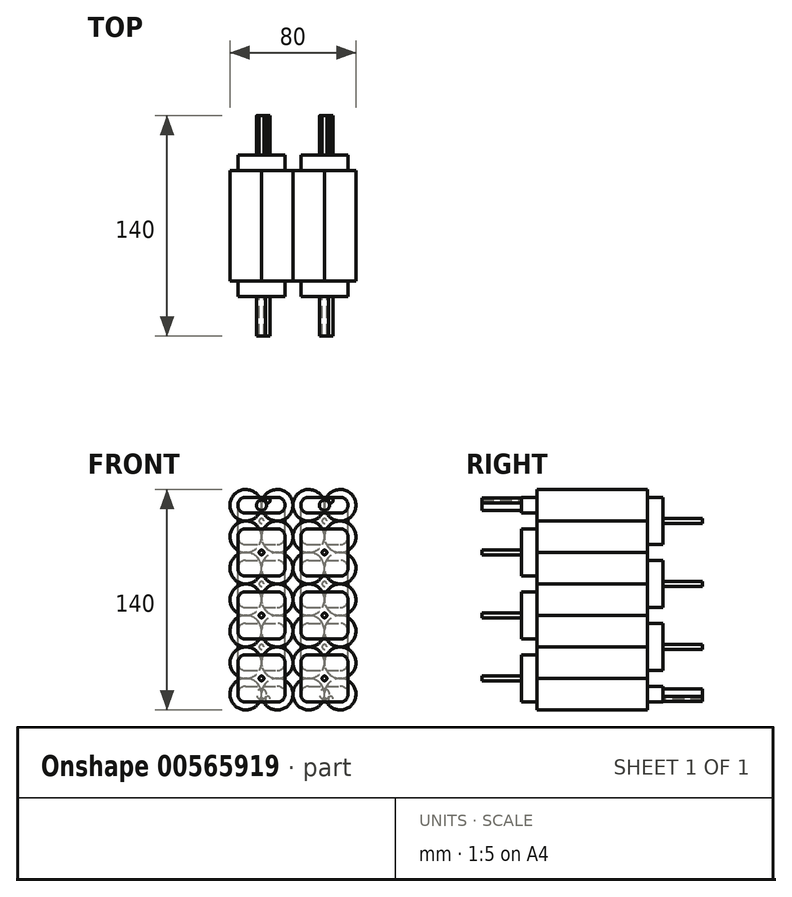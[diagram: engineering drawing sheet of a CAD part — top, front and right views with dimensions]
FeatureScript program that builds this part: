
annotation { "Feature Type Name" : "Feature", "Feature Type Description" : "" }
export const myFeature = defineFeature(function(context is Context, id is Id, definition is map)
    precondition{}
    {
        {
            var Q0;
            Q0=qCreatedBy(makeId("Front.planeOp"),FACE);
            var sketch = newSketch(context, id + "F0", { "sketchPlane" : qUnion([Q0])});
            skCircle(sketch, "E0", {"center": v(10, 10) * mm, "radius": 10 * mm});
            skCircle(sketch, "E1", {"center": v(30, 10) * mm, "radius": 10 * mm});
            skCircle(sketch, "E2", {"center": v(50, 10) * mm, "radius": 10 * mm});
            skCircle(sketch, "E3", {"center": v(70, 10) * mm, "radius": 10 * mm});
            skCircle(sketch, "E4", {"center": v(10, 30) * mm, "radius": 10 * mm});
            skCircle(sketch, "E5", {"center": v(30, 30) * mm, "radius": 10 * mm});
            skCircle(sketch, "E6", {"center": v(50, 30) * mm, "radius": 10 * mm});
            skCircle(sketch, "E7", {"center": v(70, 30) * mm, "radius": 10 * mm});
            skCircle(sketch, "E8", {"center": v(10, 50) * mm, "radius": 10 * mm});
            skCircle(sketch, "E9", {"center": v(30, 50) * mm, "radius": 10 * mm});
            skCircle(sketch, "E10", {"center": v(50, 50) * mm, "radius": 10 * mm});
            skCircle(sketch, "E11", {"center": v(70, 50) * mm, "radius": 10 * mm});
            skCircle(sketch, "E12", {"center": v(10, 70) * mm, "radius": 10 * mm});
            skCircle(sketch, "E13", {"center": v(30, 70) * mm, "radius": 10 * mm});
            skCircle(sketch, "E14", {"center": v(50, 70) * mm, "radius": 10 * mm});
            skCircle(sketch, "E15", {"center": v(70, 70) * mm, "radius": 10 * mm});
            skCircle(sketch, "E16", {"center": v(10, 90) * mm, "radius": 10 * mm});
            skCircle(sketch, "E17", {"center": v(30, 90) * mm, "radius": 10 * mm});
            skCircle(sketch, "E18", {"center": v(50, 90) * mm, "radius": 10 * mm});
            skCircle(sketch, "E19", {"center": v(70, 90) * mm, "radius": 10 * mm});
            skCircle(sketch, "E20", {"center": v(10, 110) * mm, "radius": 10 * mm});
            skCircle(sketch, "E21", {"center": v(30, 110) * mm, "radius": 10 * mm});
            skCircle(sketch, "E22", {"center": v(50, 110) * mm, "radius": 10 * mm});
            skCircle(sketch, "E23", {"center": v(70, 110) * mm, "radius": 10 * mm});
            skCircle(sketch, "E24", {"center": v(10, 130) * mm, "radius": 10 * mm});
            skCircle(sketch, "E25", {"center": v(30, 130) * mm, "radius": 10 * mm});
            skCircle(sketch, "E26", {"center": v(50, 130) * mm, "radius": 10 * mm});
            skCircle(sketch, "E27", {"center": v(70, 130) * mm, "radius": 10 * mm});
            skSolve(sketch);
        }
        {
            var Q0;
            Q0=qSketchRegion(id+"F0",true);
            extrude(context, id + "F1", {"entities" : qUnion([Q0]), "depth" : 70 * mm, "offsetDistance" : 25 * mm});
        }
        {
            var Q0;
            Q0=makeQuery(id+"F1.opExtrude","CAP_FACE",FACE,{"disambiguationData":[OSD([sQuery(id+"F0.wireOp",EDGE,"E27")])],"isStart":false});
            var sketch = newSketch(context, id + "F2", { "sketchPlane" : qUnion([Q0])});
            skLineSegment(sketch, "E28.bottom", {"start": v(35, 5) * mm, "end": v(5, 5) * mm});
            skLineSegment(sketch, "E28.top", {"start": v(35, 35) * mm, "end": v(5, 35) * mm});
            skLineSegment(sketch, "E28.left", {"start": v(35, 5) * mm, "end": v(35, 35) * mm});
            skLineSegment(sketch, "E28.right", {"start": v(5, 5) * mm, "end": v(5, 35) * mm});
            skPoint(sketch, "E28.middle", {"position": v(20, 20) * mm});
            skLineSegment(sketch, "E29.bottom", {"start": v(75, 5) * mm, "end": v(45, 5) * mm});
            skLineSegment(sketch, "E29.top", {"start": v(75, 35) * mm, "end": v(45, 35) * mm});
            skLineSegment(sketch, "E29.left", {"start": v(75, 5) * mm, "end": v(75, 35) * mm});
            skLineSegment(sketch, "E29.right", {"start": v(45, 5) * mm, "end": v(45, 35) * mm});
            skPoint(sketch, "E29.middle", {"position": v(60, 20) * mm});
            skLineSegment(sketch, "E30.bottom", {"start": v(35, 45) * mm, "end": v(5, 45) * mm});
            skLineSegment(sketch, "E30.top", {"start": v(35, 75) * mm, "end": v(5, 75) * mm});
            skLineSegment(sketch, "E30.left", {"start": v(35, 45) * mm, "end": v(35, 75) * mm});
            skLineSegment(sketch, "E30.right", {"start": v(5, 45) * mm, "end": v(5, 75) * mm});
            skPoint(sketch, "E30.middle", {"position": v(20, 60) * mm});
            skLineSegment(sketch, "E31.bottom", {"start": v(75, 45) * mm, "end": v(45, 45) * mm});
            skLineSegment(sketch, "E31.top", {"start": v(75, 75) * mm, "end": v(45, 75) * mm});
            skLineSegment(sketch, "E31.left", {"start": v(75, 45) * mm, "end": v(75, 75) * mm});
            skLineSegment(sketch, "E31.right", {"start": v(45, 45) * mm, "end": v(45, 75) * mm});
            skPoint(sketch, "E31.middle", {"position": v(60, 60) * mm});
            skLineSegment(sketch, "E32.bottom", {"start": v(35, 85) * mm, "end": v(5, 85) * mm});
            skLineSegment(sketch, "E32.top", {"start": v(35, 115) * mm, "end": v(5, 115) * mm});
            skLineSegment(sketch, "E32.left", {"start": v(35, 85) * mm, "end": v(35, 115) * mm});
            skLineSegment(sketch, "E32.right", {"start": v(5, 85) * mm, "end": v(5, 115) * mm});
            skPoint(sketch, "E32.middle", {"position": v(20, 100) * mm});
            skLineSegment(sketch, "E33.bottom", {"start": v(75, 85) * mm, "end": v(45, 85) * mm});
            skLineSegment(sketch, "E33.top", {"start": v(75, 115) * mm, "end": v(45, 115) * mm});
            skLineSegment(sketch, "E33.left", {"start": v(75, 85) * mm, "end": v(75, 115) * mm});
            skLineSegment(sketch, "E33.right", {"start": v(45, 85) * mm, "end": v(45, 115) * mm});
            skPoint(sketch, "E33.middle", {"position": v(60, 100) * mm});
            skLineSegment(sketch, "E34.bottom", {"start": v(35, 125) * mm, "end": v(5, 125) * mm});
            skLineSegment(sketch, "E34.top", {"start": v(35, 135) * mm, "end": v(5, 135) * mm});
            skLineSegment(sketch, "E34.left", {"start": v(35, 125) * mm, "end": v(35, 135) * mm});
            skLineSegment(sketch, "E34.right", {"start": v(5, 125) * mm, "end": v(5, 135) * mm});
            skPoint(sketch, "E34.middle", {"position": v(20, 130) * mm});
            skLineSegment(sketch, "E35.bottom", {"start": v(75, 125) * mm, "end": v(45, 125) * mm});
            skLineSegment(sketch, "E35.top", {"start": v(75, 135) * mm, "end": v(45, 135) * mm});
            skLineSegment(sketch, "E35.left", {"start": v(75, 125) * mm, "end": v(75, 135) * mm});
            skLineSegment(sketch, "E35.right", {"start": v(45, 125) * mm, "end": v(45, 135) * mm});
            skPoint(sketch, "E35.middle", {"position": v(60, 130) * mm});
            skSolve(sketch);
        }
        {
            var Q0;
            Q0 = qSketchRegion(id + "F2", true);
            extrude(context, id + "F3", {"entities" : qUnion([Q0]), "depth" : 10 * mm, "offsetDistance" : 25 * mm});
        }
        {
            var Q0;
            Q0=makeQuery(id+"F1.opExtrude","CAP_FACE",FACE,{"disambiguationData":[OSD([sQuery(id+"F0.wireOp",EDGE,"E24")])],"isStart":true});
            var sketch = newSketch(context, id + "F4", { "sketchPlane" : qUnion([Q0])});
            skLineSegment(sketch, "E36.bottom", {"start": v(-45, 25) * mm, "end": v(-75, 25) * mm});
            skLineSegment(sketch, "E36.top", {"start": v(-45, 55) * mm, "end": v(-75, 55) * mm});
            skLineSegment(sketch, "E36.left", {"start": v(-45, 25) * mm, "end": v(-45, 55) * mm});
            skLineSegment(sketch, "E36.right", {"start": v(-75, 25) * mm, "end": v(-75, 55) * mm});
            skPoint(sketch, "E36.middle", {"position": v(-60, 40) * mm});
            skLineSegment(sketch, "E37.bottom", {"start": v(-5, 25) * mm, "end": v(-35, 25) * mm});
            skLineSegment(sketch, "E37.top", {"start": v(-5, 55) * mm, "end": v(-35, 55) * mm});
            skLineSegment(sketch, "E37.left", {"start": v(-5, 25) * mm, "end": v(-5, 55) * mm});
            skLineSegment(sketch, "E37.right", {"start": v(-35, 25) * mm, "end": v(-35, 55) * mm});
            skPoint(sketch, "E37.middle", {"position": v(-20, 40) * mm});
            skLineSegment(sketch, "E38.bottom", {"start": v(-45, 65) * mm, "end": v(-75, 65) * mm});
            skLineSegment(sketch, "E38.top", {"start": v(-45, 95) * mm, "end": v(-75, 95) * mm});
            skLineSegment(sketch, "E38.left", {"start": v(-45, 65) * mm, "end": v(-45, 95) * mm});
            skLineSegment(sketch, "E38.right", {"start": v(-75, 65) * mm, "end": v(-75, 95) * mm});
            skPoint(sketch, "E38.middle", {"position": v(-60, 80) * mm});
            skLineSegment(sketch, "E39.bottom", {"start": v(-5, 65) * mm, "end": v(-35, 65) * mm});
            skLineSegment(sketch, "E39.top", {"start": v(-5, 95) * mm, "end": v(-35, 95) * mm});
            skLineSegment(sketch, "E39.left", {"start": v(-5, 65) * mm, "end": v(-5, 95) * mm});
            skLineSegment(sketch, "E39.right", {"start": v(-35, 65) * mm, "end": v(-35, 95) * mm});
            skPoint(sketch, "E39.middle", {"position": v(-20, 80) * mm});
            skLineSegment(sketch, "E40.bottom", {"start": v(-45, 105) * mm, "end": v(-75, 105) * mm});
            skLineSegment(sketch, "E40.top", {"start": v(-45, 135) * mm, "end": v(-75, 135) * mm});
            skLineSegment(sketch, "E40.left", {"start": v(-45, 105) * mm, "end": v(-45, 135) * mm});
            skLineSegment(sketch, "E40.right", {"start": v(-75, 105) * mm, "end": v(-75, 135) * mm});
            skPoint(sketch, "E40.middle", {"position": v(-60, 120) * mm});
            skLineSegment(sketch, "E41.bottom", {"start": v(-5, 105) * mm, "end": v(-35, 105) * mm});
            skLineSegment(sketch, "E41.top", {"start": v(-5, 135) * mm, "end": v(-35, 135) * mm});
            skLineSegment(sketch, "E41.left", {"start": v(-5, 105) * mm, "end": v(-5, 135) * mm});
            skLineSegment(sketch, "E41.right", {"start": v(-35, 105) * mm, "end": v(-35, 135) * mm});
            skPoint(sketch, "E41.middle", {"position": v(-20, 120) * mm});
            skLineSegment(sketch, "E42.bottom", {"start": v(-45, 5) * mm, "end": v(-75, 5) * mm});
            skLineSegment(sketch, "E42.top", {"start": v(-45, 15) * mm, "end": v(-75, 15) * mm});
            skLineSegment(sketch, "E42.left", {"start": v(-45, 5) * mm, "end": v(-45, 15) * mm});
            skLineSegment(sketch, "E42.right", {"start": v(-75, 5) * mm, "end": v(-75, 15) * mm});
            skPoint(sketch, "E42.middle", {"position": v(-60, 10) * mm});
            skLineSegment(sketch, "E43.bottom", {"start": v(-5, 5) * mm, "end": v(-35, 5) * mm});
            skLineSegment(sketch, "E43.top", {"start": v(-5, 15) * mm, "end": v(-35, 15) * mm});
            skLineSegment(sketch, "E43.left", {"start": v(-5, 5) * mm, "end": v(-5, 15) * mm});
            skLineSegment(sketch, "E43.right", {"start": v(-35, 5) * mm, "end": v(-35, 15) * mm});
            skPoint(sketch, "E43.middle", {"position": v(-20, 10) * mm});
            skSolve(sketch);
        }
        {
            var Q0;
            Q0 = qSketchRegion(id + "F4", true);
            extrude(context, id + "F5", {"entities" : qUnion([Q0]), "depth" : 10 * mm, "offsetDistance" : 25 * mm});
        }
        {
            var Q0;
            Q0=makeQuery(id+"F3.opExtrude","SWEPT_EDGE",EDGE,{"disambiguationData":[OSD([sQuery(id+"F2.wireOp",EDGE,"E35.top"),sQuery(id+"F2.wireOp",EDGE,"E35.left")])]});
            var Q1;
            Q1=makeQuery(id+"F3.opExtrude","SWEPT_EDGE",EDGE,{"disambiguationData":[OSD([sQuery(id+"F2.wireOp",EDGE,"E35.bottom"),sQuery(id+"F2.wireOp",EDGE,"E35.left")])]});
            var Q2;
            Q2=makeQuery(id+"F3.opExtrude","SWEPT_EDGE",EDGE,{"disambiguationData":[OSD([sQuery(id+"F2.wireOp",EDGE,"E33.top"),sQuery(id+"F2.wireOp",EDGE,"E33.left")])]});
            var Q3;
            Q3=makeQuery(id+"F3.opExtrude","SWEPT_EDGE",EDGE,{"disambiguationData":[OSD([sQuery(id+"F2.wireOp",EDGE,"E33.bottom"),sQuery(id+"F2.wireOp",EDGE,"E33.left")])]});
            var Q4;
            Q4=makeQuery(id+"F3.opExtrude","SWEPT_EDGE",EDGE,{"disambiguationData":[OSD([sQuery(id+"F2.wireOp",EDGE,"E33.top"),sQuery(id+"F2.wireOp",EDGE,"E33.right")])]});
            var Q5;
            Q5=makeQuery(id+"F3.opExtrude","SWEPT_EDGE",EDGE,{"disambiguationData":[OSD([sQuery(id+"F2.wireOp",EDGE,"E35.top"),sQuery(id+"F2.wireOp",EDGE,"E35.right")])]});
            var Q6;
            Q6=makeQuery(id+"F3.opExtrude","SWEPT_EDGE",EDGE,{"disambiguationData":[OSD([sQuery(id+"F2.wireOp",EDGE,"E34.top"),sQuery(id+"F2.wireOp",EDGE,"E34.left")])]});
            var Q7;
            Q7=makeQuery(id+"F3.opExtrude","SWEPT_EDGE",EDGE,{"disambiguationData":[OSD([sQuery(id+"F2.wireOp",EDGE,"E34.top"),sQuery(id+"F2.wireOp",EDGE,"E34.right")])]});
            var Q8;
            Q8=makeQuery(id+"F3.opExtrude","SWEPT_EDGE",EDGE,{"disambiguationData":[OSD([sQuery(id+"F2.wireOp",EDGE,"E32.top"),sQuery(id+"F2.wireOp",EDGE,"E32.right")])]});
            var Q9;
            Q9=makeQuery(id+"F3.opExtrude","SWEPT_EDGE",EDGE,{"disambiguationData":[OSD([sQuery(id+"F2.wireOp",EDGE,"E32.top"),sQuery(id+"F2.wireOp",EDGE,"E32.left")])]});
            var Q10;
            Q10=makeQuery(id+"F3.opExtrude","SWEPT_EDGE",EDGE,{"disambiguationData":[OSD([sQuery(id+"F2.wireOp",EDGE,"E30.top"),sQuery(id+"F2.wireOp",EDGE,"E30.right")])]});
            var Q11;
            Q11=makeQuery(id+"F3.opExtrude","SWEPT_EDGE",EDGE,{"disambiguationData":[OSD([sQuery(id+"F2.wireOp",EDGE,"E30.top"),sQuery(id+"F2.wireOp",EDGE,"E30.left")])]});
            var Q12;
            Q12=makeQuery(id+"F3.opExtrude","SWEPT_EDGE",EDGE,{"disambiguationData":[OSD([sQuery(id+"F2.wireOp",EDGE,"E31.top"),sQuery(id+"F2.wireOp",EDGE,"E31.right")])]});
            var Q13;
            Q13=makeQuery(id+"F3.opExtrude","SWEPT_EDGE",EDGE,{"disambiguationData":[OSD([sQuery(id+"F2.wireOp",EDGE,"E31.top"),sQuery(id+"F2.wireOp",EDGE,"E31.left")])]});
            var Q14;
            Q14=makeQuery(id+"F3.opExtrude","SWEPT_EDGE",EDGE,{"disambiguationData":[OSD([sQuery(id+"F2.wireOp",EDGE,"E31.bottom"),sQuery(id+"F2.wireOp",EDGE,"E31.left")])]});
            var Q15;
            Q15=makeQuery(id+"F3.opExtrude","SWEPT_EDGE",EDGE,{"disambiguationData":[OSD([sQuery(id+"F2.wireOp",EDGE,"E30.bottom"),sQuery(id+"F2.wireOp",EDGE,"E30.left")])]});
            var Q16;
            Q16=makeQuery(id+"F3.opExtrude","SWEPT_EDGE",EDGE,{"disambiguationData":[OSD([sQuery(id+"F2.wireOp",EDGE,"E34.bottom"),sQuery(id+"F2.wireOp",EDGE,"E34.left")])]});
            var Q17;
            Q17=makeQuery(id+"F3.opExtrude","SWEPT_EDGE",EDGE,{"disambiguationData":[OSD([sQuery(id+"F2.wireOp",EDGE,"E32.bottom"),sQuery(id+"F2.wireOp",EDGE,"E32.left")])]});
            var Q18;
            Q18=makeQuery(id+"F3.opExtrude","SWEPT_EDGE",EDGE,{"disambiguationData":[OSD([sQuery(id+"F2.wireOp",EDGE,"E28.top"),sQuery(id+"F2.wireOp",EDGE,"E28.right")])]});
            var Q19;
            Q19=makeQuery(id+"F3.opExtrude","SWEPT_EDGE",EDGE,{"disambiguationData":[OSD([sQuery(id+"F2.wireOp",EDGE,"E28.top"),sQuery(id+"F2.wireOp",EDGE,"E28.left")])]});
            var Q20;
            Q20=makeQuery(id+"F3.opExtrude","SWEPT_EDGE",EDGE,{"disambiguationData":[OSD([sQuery(id+"F2.wireOp",EDGE,"E29.top"),sQuery(id+"F2.wireOp",EDGE,"E29.right")])]});
            var Q21;
            Q21=makeQuery(id+"F3.opExtrude","SWEPT_EDGE",EDGE,{"disambiguationData":[OSD([sQuery(id+"F2.wireOp",EDGE,"E29.top"),sQuery(id+"F2.wireOp",EDGE,"E29.left")])]});
            var Q22;
            Q22=makeQuery(id+"F3.opExtrude","SWEPT_EDGE",EDGE,{"disambiguationData":[OSD([sQuery(id+"F2.wireOp",EDGE,"E29.bottom"),sQuery(id+"F2.wireOp",EDGE,"E29.left")])]});
            var Q23;
            Q23=makeQuery(id+"F3.opExtrude","SWEPT_EDGE",EDGE,{"disambiguationData":[OSD([sQuery(id+"F2.wireOp",EDGE,"E28.bottom"),sQuery(id+"F2.wireOp",EDGE,"E28.left")])]});
            var Q24;
            Q24=makeQuery(id+"F3.opExtrude","SWEPT_EDGE",EDGE,{"disambiguationData":[OSD([sQuery(id+"F2.wireOp",EDGE,"E34.bottom"),sQuery(id+"F2.wireOp",EDGE,"E34.right")])]});
            var Q25;
            Q25=makeQuery(id+"F3.opExtrude","SWEPT_EDGE",EDGE,{"disambiguationData":[OSD([sQuery(id+"F2.wireOp",EDGE,"E35.bottom"),sQuery(id+"F2.wireOp",EDGE,"E35.right")])]});
            var Q26;
            Q26=makeQuery(id+"F3.opExtrude","SWEPT_EDGE",EDGE,{"disambiguationData":[OSD([sQuery(id+"F2.wireOp",EDGE,"E32.bottom"),sQuery(id+"F2.wireOp",EDGE,"E32.right")])]});
            var Q27;
            Q27=makeQuery(id+"F3.opExtrude","SWEPT_EDGE",EDGE,{"disambiguationData":[OSD([sQuery(id+"F2.wireOp",EDGE,"E33.bottom"),sQuery(id+"F2.wireOp",EDGE,"E33.right")])]});
            var Q28;
            Q28=makeQuery(id+"F3.opExtrude","SWEPT_EDGE",EDGE,{"disambiguationData":[OSD([sQuery(id+"F2.wireOp",EDGE,"E30.bottom"),sQuery(id+"F2.wireOp",EDGE,"E30.right")])]});
            var Q29;
            Q29=makeQuery(id+"F3.opExtrude","SWEPT_EDGE",EDGE,{"disambiguationData":[OSD([sQuery(id+"F2.wireOp",EDGE,"E31.bottom"),sQuery(id+"F2.wireOp",EDGE,"E31.right")])]});
            var Q30;
            Q30=makeQuery(id+"F3.opExtrude","SWEPT_EDGE",EDGE,{"disambiguationData":[OSD([sQuery(id+"F2.wireOp",EDGE,"E28.bottom"),sQuery(id+"F2.wireOp",EDGE,"E28.right")])]});
            var Q31;
            Q31=makeQuery(id+"F3.opExtrude","SWEPT_EDGE",EDGE,{"disambiguationData":[OSD([sQuery(id+"F2.wireOp",EDGE,"E29.bottom"),sQuery(id+"F2.wireOp",EDGE,"E29.right")])]});
            var Q32;
            Q32=makeQuery(id+"F5.opExtrude","SWEPT_EDGE",EDGE,{"disambiguationData":[OSD([sQuery(id+"F4.wireOp",EDGE,"E43.bottom"),sQuery(id+"F4.wireOp",EDGE,"E43.left")])]});
            var Q33;
            Q33=makeQuery(id+"F5.opExtrude","SWEPT_EDGE",EDGE,{"disambiguationData":[OSD([sQuery(id+"F4.wireOp",EDGE,"E37.bottom"),sQuery(id+"F4.wireOp",EDGE,"E37.left")])]});
            var Q34;
            Q34=makeQuery(id+"F5.opExtrude","SWEPT_EDGE",EDGE,{"disambiguationData":[OSD([sQuery(id+"F4.wireOp",EDGE,"E43.bottom"),sQuery(id+"F4.wireOp",EDGE,"E43.right")])]});
            var Q35;
            Q35=makeQuery(id+"F5.opExtrude","SWEPT_EDGE",EDGE,{"disambiguationData":[OSD([sQuery(id+"F4.wireOp",EDGE,"E42.bottom"),sQuery(id+"F4.wireOp",EDGE,"E42.left")])]});
            var Q36;
            Q36=makeQuery(id+"F5.opExtrude","SWEPT_EDGE",EDGE,{"disambiguationData":[OSD([sQuery(id+"F4.wireOp",EDGE,"E42.top"),sQuery(id+"F4.wireOp",EDGE,"E42.left")])]});
            var Q37;
            Q37=makeQuery(id+"F5.opExtrude","SWEPT_EDGE",EDGE,{"disambiguationData":[OSD([sQuery(id+"F4.wireOp",EDGE,"E37.bottom"),sQuery(id+"F4.wireOp",EDGE,"E37.right")])]});
            var Q38;
            Q38=makeQuery(id+"F5.opExtrude","SWEPT_EDGE",EDGE,{"disambiguationData":[OSD([sQuery(id+"F4.wireOp",EDGE,"E36.bottom"),sQuery(id+"F4.wireOp",EDGE,"E36.left")])]});
            var Q39;
            Q39=makeQuery(id+"F5.opExtrude","SWEPT_EDGE",EDGE,{"disambiguationData":[OSD([sQuery(id+"F4.wireOp",EDGE,"E42.bottom"),sQuery(id+"F4.wireOp",EDGE,"E42.right")])]});
            var Q40;
            Q40=makeQuery(id+"F5.opExtrude","SWEPT_EDGE",EDGE,{"disambiguationData":[OSD([sQuery(id+"F4.wireOp",EDGE,"E36.bottom"),sQuery(id+"F4.wireOp",EDGE,"E36.right")])]});
            var Q41;
            Q41=makeQuery(id+"F5.opExtrude","SWEPT_EDGE",EDGE,{"disambiguationData":[OSD([sQuery(id+"F4.wireOp",EDGE,"E36.top"),sQuery(id+"F4.wireOp",EDGE,"E36.left")])]});
            var Q42;
            Q42=makeQuery(id+"F5.opExtrude","SWEPT_EDGE",EDGE,{"disambiguationData":[OSD([sQuery(id+"F4.wireOp",EDGE,"E38.bottom"),sQuery(id+"F4.wireOp",EDGE,"E38.right")])]});
            var Q43;
            Q43=makeQuery(id+"F5.opExtrude","SWEPT_EDGE",EDGE,{"disambiguationData":[OSD([sQuery(id+"F4.wireOp",EDGE,"E38.bottom"),sQuery(id+"F4.wireOp",EDGE,"E38.left")])]});
            var Q44;
            Q44=makeQuery(id+"F5.opExtrude","SWEPT_EDGE",EDGE,{"disambiguationData":[OSD([sQuery(id+"F4.wireOp",EDGE,"E39.bottom"),sQuery(id+"F4.wireOp",EDGE,"E39.right")])]});
            var Q45;
            Q45=makeQuery(id+"F5.opExtrude","SWEPT_EDGE",EDGE,{"disambiguationData":[OSD([sQuery(id+"F4.wireOp",EDGE,"E38.top"),sQuery(id+"F4.wireOp",EDGE,"E38.left")])]});
            var Q46;
            Q46=makeQuery(id+"F5.opExtrude","SWEPT_EDGE",EDGE,{"disambiguationData":[OSD([sQuery(id+"F4.wireOp",EDGE,"E39.bottom"),sQuery(id+"F4.wireOp",EDGE,"E39.left")])]});
            var Q47;
            Q47=makeQuery(id+"F5.opExtrude","SWEPT_EDGE",EDGE,{"disambiguationData":[OSD([sQuery(id+"F4.wireOp",EDGE,"E37.top"),sQuery(id+"F4.wireOp",EDGE,"E37.left")])]});
            var Q48;
            Q48=makeQuery(id+"F5.opExtrude","SWEPT_EDGE",EDGE,{"disambiguationData":[OSD([sQuery(id+"F4.wireOp",EDGE,"E43.top"),sQuery(id+"F4.wireOp",EDGE,"E43.left")])]});
            var Q49;
            Q49=makeQuery(id+"F5.opExtrude","SWEPT_EDGE",EDGE,{"disambiguationData":[OSD([sQuery(id+"F4.wireOp",EDGE,"E39.top"),sQuery(id+"F4.wireOp",EDGE,"E39.left")])]});
            var Q50;
            Q50=makeQuery(id+"F5.opExtrude","SWEPT_EDGE",EDGE,{"disambiguationData":[OSD([sQuery(id+"F4.wireOp",EDGE,"E41.bottom"),sQuery(id+"F4.wireOp",EDGE,"E41.left")])]});
            var Q51;
            Q51=makeQuery(id+"F5.opExtrude","SWEPT_EDGE",EDGE,{"disambiguationData":[OSD([sQuery(id+"F4.wireOp",EDGE,"E41.bottom"),sQuery(id+"F4.wireOp",EDGE,"E41.right")])]});
            var Q52;
            Q52=makeQuery(id+"F5.opExtrude","SWEPT_EDGE",EDGE,{"disambiguationData":[OSD([sQuery(id+"F4.wireOp",EDGE,"E40.bottom"),sQuery(id+"F4.wireOp",EDGE,"E40.left")])]});
            var Q53;
            Q53=makeQuery(id+"F5.opExtrude","SWEPT_EDGE",EDGE,{"disambiguationData":[OSD([sQuery(id+"F4.wireOp",EDGE,"E40.bottom"),sQuery(id+"F4.wireOp",EDGE,"E40.right")])]});
            var Q54;
            Q54=makeQuery(id+"F5.opExtrude","SWEPT_EDGE",EDGE,{"disambiguationData":[OSD([sQuery(id+"F4.wireOp",EDGE,"E40.top"),sQuery(id+"F4.wireOp",EDGE,"E40.left")])]});
            var Q55;
            Q55=makeQuery(id+"F5.opExtrude","SWEPT_EDGE",EDGE,{"disambiguationData":[OSD([sQuery(id+"F4.wireOp",EDGE,"E41.top"),sQuery(id+"F4.wireOp",EDGE,"E41.left")])]});
            var Q56;
            Q56=makeQuery(id+"F5.opExtrude","SWEPT_EDGE",EDGE,{"disambiguationData":[OSD([sQuery(id+"F4.wireOp",EDGE,"E41.top"),sQuery(id+"F4.wireOp",EDGE,"E41.right")])]});
            var Q57;
            Q57=makeQuery(id+"F5.opExtrude","SWEPT_EDGE",EDGE,{"disambiguationData":[OSD([sQuery(id+"F4.wireOp",EDGE,"E40.top"),sQuery(id+"F4.wireOp",EDGE,"E40.right")])]});
            var Q58;
            Q58=makeQuery(id+"F5.opExtrude","SWEPT_EDGE",EDGE,{"disambiguationData":[OSD([sQuery(id+"F4.wireOp",EDGE,"E39.top"),sQuery(id+"F4.wireOp",EDGE,"E39.right")])]});
            var Q59;
            Q59=makeQuery(id+"F5.opExtrude","SWEPT_EDGE",EDGE,{"disambiguationData":[OSD([sQuery(id+"F4.wireOp",EDGE,"E38.top"),sQuery(id+"F4.wireOp",EDGE,"E38.right")])]});
            var Q60;
            Q60=makeQuery(id+"F5.opExtrude","SWEPT_EDGE",EDGE,{"disambiguationData":[OSD([sQuery(id+"F4.wireOp",EDGE,"E36.top"),sQuery(id+"F4.wireOp",EDGE,"E36.right")])]});
            var Q61;
            Q61=makeQuery(id+"F5.opExtrude","SWEPT_EDGE",EDGE,{"disambiguationData":[OSD([sQuery(id+"F4.wireOp",EDGE,"E37.top"),sQuery(id+"F4.wireOp",EDGE,"E37.right")])]});
            var Q62;
            Q62=makeQuery(id+"F5.opExtrude","SWEPT_EDGE",EDGE,{"disambiguationData":[OSD([sQuery(id+"F4.wireOp",EDGE,"E43.top"),sQuery(id+"F4.wireOp",EDGE,"E43.right")])]});
            var Q63;
            Q63=makeQuery(id+"F5.opExtrude","SWEPT_EDGE",EDGE,{"disambiguationData":[OSD([sQuery(id+"F4.wireOp",EDGE,"E42.top"),sQuery(id+"F4.wireOp",EDGE,"E42.right")])]});
            fillet(context, id + "F6", {"entities" : qUnion([Q0, Q1, Q2, Q3, Q4, Q5, Q6, Q7, Q8, Q9, Q10, Q11, Q12, Q13, Q14, Q15, Q16, Q17, Q18, Q19, Q20, Q21, Q22, Q23, Q24, Q25, Q26, Q27, Q28, Q29, Q30, Q31, Q32, Q33, Q34, Q35, Q36, Q37, Q38, Q39, Q40, Q41, Q42, Q43, Q44, Q45, Q46, Q47, Q48, Q49, Q50, Q51, Q52, Q53, Q54, Q55, Q56, Q57, Q58, Q59, Q60, Q61, Q62, Q63]), "radius" : 5 * mm, "tangentPropagation" : true, "allowEdgeOverflow" : false});
        }
        {
            var Q0;
            Q0=makeQuery(id+"F5.opExtrude","CAP_FACE",FACE,{"disambiguationData":[OSD([sQuery(id+"F4.wireOp",EDGE,"E40.bottom"),sQuery(id+"F4.wireOp",EDGE,"E40.top"),sQuery(id+"F4.wireOp",EDGE,"E40.left"),sQuery(id+"F4.wireOp",EDGE,"E40.right")])],"isStart":false});
            var sketch = newSketch(context, id + "F7", { "sketchPlane" : qUnion([Q0])});
            skCircle(sketch, "E44", {"center": v(-60, 120) * mm, "radius": 1.5 * mm});
            skCircle(sketch, "E45", {"center": v(-20, 120) * mm, "radius": 1.5 * mm});
            skCircle(sketch, "E46", {"center": v(-60, 80) * mm, "radius": 1.5 * mm});
            skCircle(sketch, "E47", {"center": v(-20, 80) * mm, "radius": 1.5 * mm});
            skCircle(sketch, "E48", {"center": v(-60, 40) * mm, "radius": 1.5 * mm});
            skCircle(sketch, "E49", {"center": v(-20, 40) * mm, "radius": 1.5 * mm});
            skCircle(sketch, "E50", {"center": v(-60, 10) * mm, "radius": 3.25 * mm});
            skCircle(sketch, "E51", {"center": v(-20, 10) * mm, "radius": 3.25 * mm});
            skCircle(sketch, "E52", {"center": v(-64, 7) * mm, "radius": 1.5 * mm});
            skCircle(sketch, "E53", {"center": v(-24, 7) * mm, "radius": 1.5 * mm});
            skSolve(sketch);
        }
        {
            var Q0;
            Q0 = qSketchRegion(id + "F7", true);
            extrude(context, id + "F8", {"entities" : qUnion([Q0]), "depth" : 25 * mm, "offsetDistance" : 25 * mm});
        }
        {
            var Q0;
            Q0=makeQuery(id+"F3.opExtrude","CAP_FACE",FACE,{"disambiguationData":[OSD([sQuery(id+"F2.wireOp",EDGE,"E30.bottom"),sQuery(id+"F2.wireOp",EDGE,"E30.top"),sQuery(id+"F2.wireOp",EDGE,"E30.left"),sQuery(id+"F2.wireOp",EDGE,"E30.right")])],"isStart":false});
            var sketch = newSketch(context, id + "F9", { "sketchPlane" : qUnion([Q0])});
            skCircle(sketch, "E54", {"center": v(20, 130) * mm, "radius": 3.25 * mm});
            skCircle(sketch, "E55", {"center": v(60, 130) * mm, "radius": 3.25 * mm});
            skCircle(sketch, "E56", {"center": v(20, 100) * mm, "radius": 1.5 * mm});
            skCircle(sketch, "E57", {"center": v(60, 100) * mm, "radius": 1.5 * mm});
            skCircle(sketch, "E58", {"center": v(20, 60) * mm, "radius": 1.5 * mm});
            skCircle(sketch, "E59", {"center": v(60, 60) * mm, "radius": 1.5 * mm});
            skCircle(sketch, "E60", {"center": v(20, 20) * mm, "radius": 1.5 * mm});
            skCircle(sketch, "E61", {"center": v(60, 20) * mm, "radius": 1.5 * mm});
            skCircle(sketch, "E62", {"center": v(24, 133) * mm, "radius": 1.5 * mm});
            skCircle(sketch, "E63", {"center": v(64, 133) * mm, "radius": 1.5 * mm});
            skSolve(sketch);
        }
        {
            var Q0;
            Q0 = qSketchRegion(id + "F9", true);
            extrude(context, id + "F10", {"entities" : qUnion([Q0]), "depth" : 25 * mm, "offsetDistance" : 25 * mm});
        }
    });
